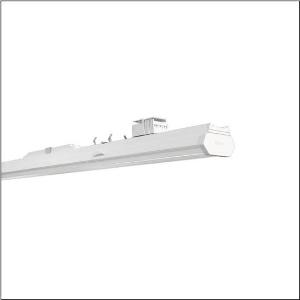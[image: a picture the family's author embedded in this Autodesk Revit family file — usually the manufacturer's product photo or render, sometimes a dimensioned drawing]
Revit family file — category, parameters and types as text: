
# Revit family: licross_r__21_protected_ho_52td11dn4dxs_f76a
name_source: partatom
category: Lighting Fixtures
units: mm (PartAtom-declared; Revit-internal decimal feet)

## family parameters
Cut with Voids When Loaded = No
Host = Face
Light Source = No
Part Type = Normal
Room Calculation Point = No
Round Connector Dimension = Use Diameter
Shared = No

## types (1)
- --- (1 x LED, 13000 lm, 73.1 W, 4000K)
    Apparent Load = 73 VA
    CIE Flux Codes = 84 94 98 99 100
    Color Rendering = 80
    Color Temperature = 4000K
    Default Elevation = 1800 mm
    Description = Licross® 21 Protected HO, luminaire insert, of sheet steel, galvanised, coil coated, white, length: 1.500mm, width: 90mm, height: 103mm, LED rated luminous flux: 13.000lm, light colour: 840, control gear: DALI 2, with plug, 5-pole, with phase selection, mains connection: 220..240V, AC, 50/60Hz, rated input power: 73W, halogen-free wiring, primary light control with lens, of plastic, primary optical cover: cover, of PMMA, light emission: direct distribution, primary light characteristic: symmetric, protection rating (complete): IP54, insulation class (complete): insulation class I (protective earthing), certification: CE, ENEC, VDE, UKCA, protection symbol: D if used in an environment with non-conductive dust loads with corresponding accessories, impact resistance: IK06, permissible ambient temperature for indoor applications: -25..+40°C, corresponds to IFS (International Featured Standards) requirements for safety and quality in the food industry, reducing of maximum allowable ambient temperature of 5°C with ceiling mounting, LABS conformity tested according to VDMA 24364:2018-05, packaging unit: 1 piece
    Height = 92 mm
    Lamp = 1 x LED
    Lamp Light Flux = 13000 lm
    Lamp Power = 73.1 W
    Lamp count = 1
    Length = 1500 mm
    Luminous efficacy = 178 lm/W
    Manufacturer = Siteco
    ModVariant = No
    Model = 52TD11DN4DXS
    Mounting Place = Ceiling
    Mounting Type = Pendant
    Number of Poles = 1
    OnlyDefault = Yes
    Power Factor = 1
    Product Name = Licross® 21 Protected HO
    Product group = luminaire insert
    ProductGroupID = 901
    Protection Class = Protection class I
    Protection Degree = IP 54
    RLX_Detail_Level = 1
    RLX_Emergency_Light_Flux = 0 lm
    RLX_Emergency_Type = 0
    RLX_Emergency_Type_DB = No
    RlxData = <blob elided: 24373 chars, md5=4a6141e6>
    Socket = socket
    Standby Power = 0 W
    System Light Flux = 13000 lm
    System Power = 73 W
    Type Comments = factory setting: luminous flux: 100 % | dim-lin: 254 | 417 mA
    Type Image = l_1256148.jpg
    URL = http://relux.com
    VarID = @adj_078159
    Voltage = 0 V
    Weight = 0.00 kg
    Width = 88 mm

## geometry (parser evidence)
native form markers: Blend x4, Sweep x10
no freeform markers — native parametric forms only
